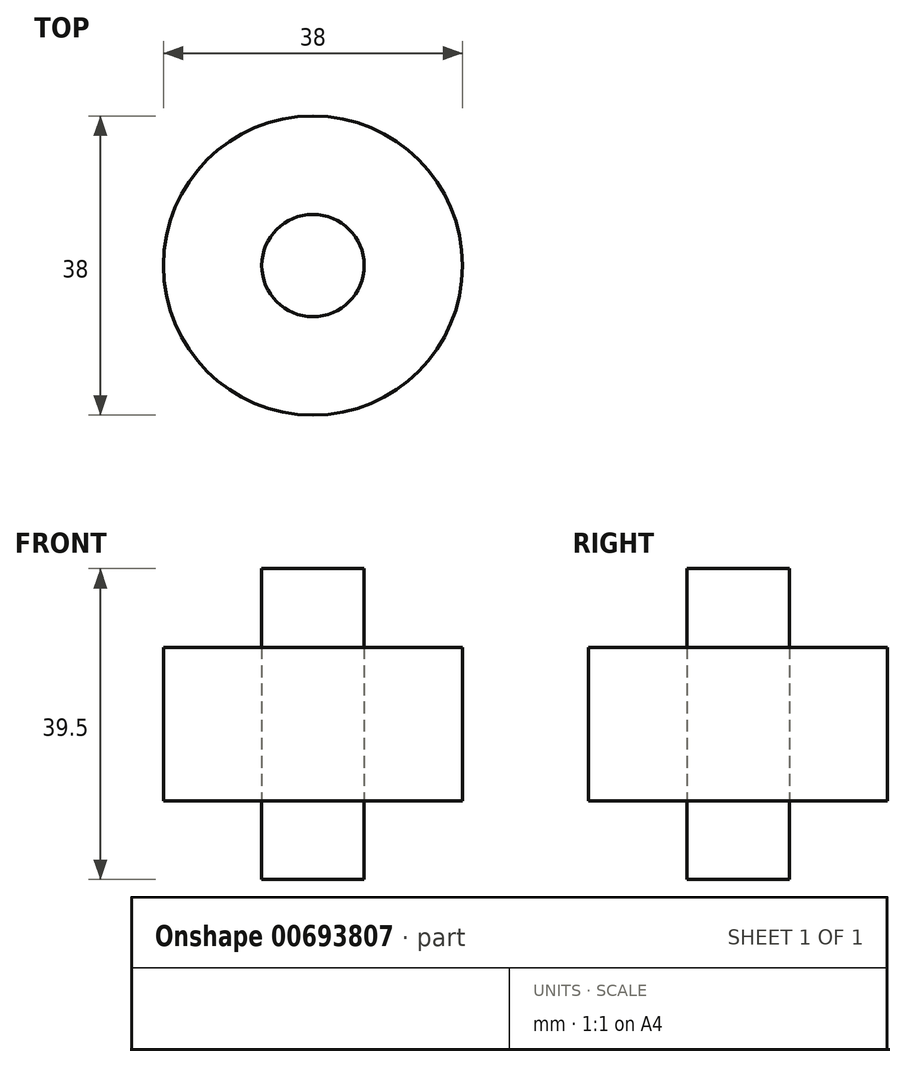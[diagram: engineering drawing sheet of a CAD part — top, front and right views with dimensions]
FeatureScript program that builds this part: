
annotation { "Feature Type Name" : "Feature", "Feature Type Description" : "" }
export const myFeature = defineFeature(function(context is Context, id is Id, definition is map)
    precondition{}
    {
        {
            var Q0;
            Q0=qCreatedBy(makeId("Top.planeOp"),FACE);
            var sketch = newSketch(context, id + "F0", { "sketchPlane" : qUnion([Q0])});
            skCircle(sketch, "E0", {"center": v(0, 0) * mm, "radius": 19 * mm});
            skSolve(sketch);
        }
        {
            var Q0;
            Q0 = qSketchRegion(id + "F0", true);
            extrude(context, id + "F1", {"entities" : qUnion([Q0]), "depth" : 19.5 * mm, "offsetDistance" : 25 * mm});
        }
        {
            var Q0;
            Q0=qCreatedBy(makeId("Top.planeOp"),FACE);
            var sketch = newSketch(context, id + "F2", { "sketchPlane" : qUnion([Q0])});
            skCircle(sketch, "E1", {"center": v(0, 0) * mm, "radius": 6.5 * mm});
            skSolve(sketch);
        }
        {
            var Q0;
            Q0=makeQuery(id+"F2.imprint","IMPRINT",FACE,{"disambiguationData":[TD([[makeQuery(id+"F2.imprint","IMPRINT",EDGE,{"derivedFrom":sQuery(id+"F2.wireOp",EDGE,"E1")}),1.0]])]});
            var Q1;
            Q1=sQuery(id+"F2.wireOp",EDGE,"q1fAnVyo-x8vg-vHDY-odOx-ZLTL4K9JfmB7");
            var Q2;
            Q2=sQuery(id+"F2.wireOp",EDGE,"E1");
            extrude(context, id + "F3", {"entities" : qUnion([Q0]), "surfaceEntities" : qUnion([Q1, Q2]), "depth" : (19.5 + 10) * mm, "offsetDistance" : 25 * mm});
        }
        {
            var Q0;
            Q0 = qSketchRegion(id + "F2", true);
            extrude(context, id + "F4", {"entities" : qUnion([Q0]), "oppositeDirection" : true, "depth" : 10 * mm, "offsetDistance" : 25 * mm});
        }
    });
